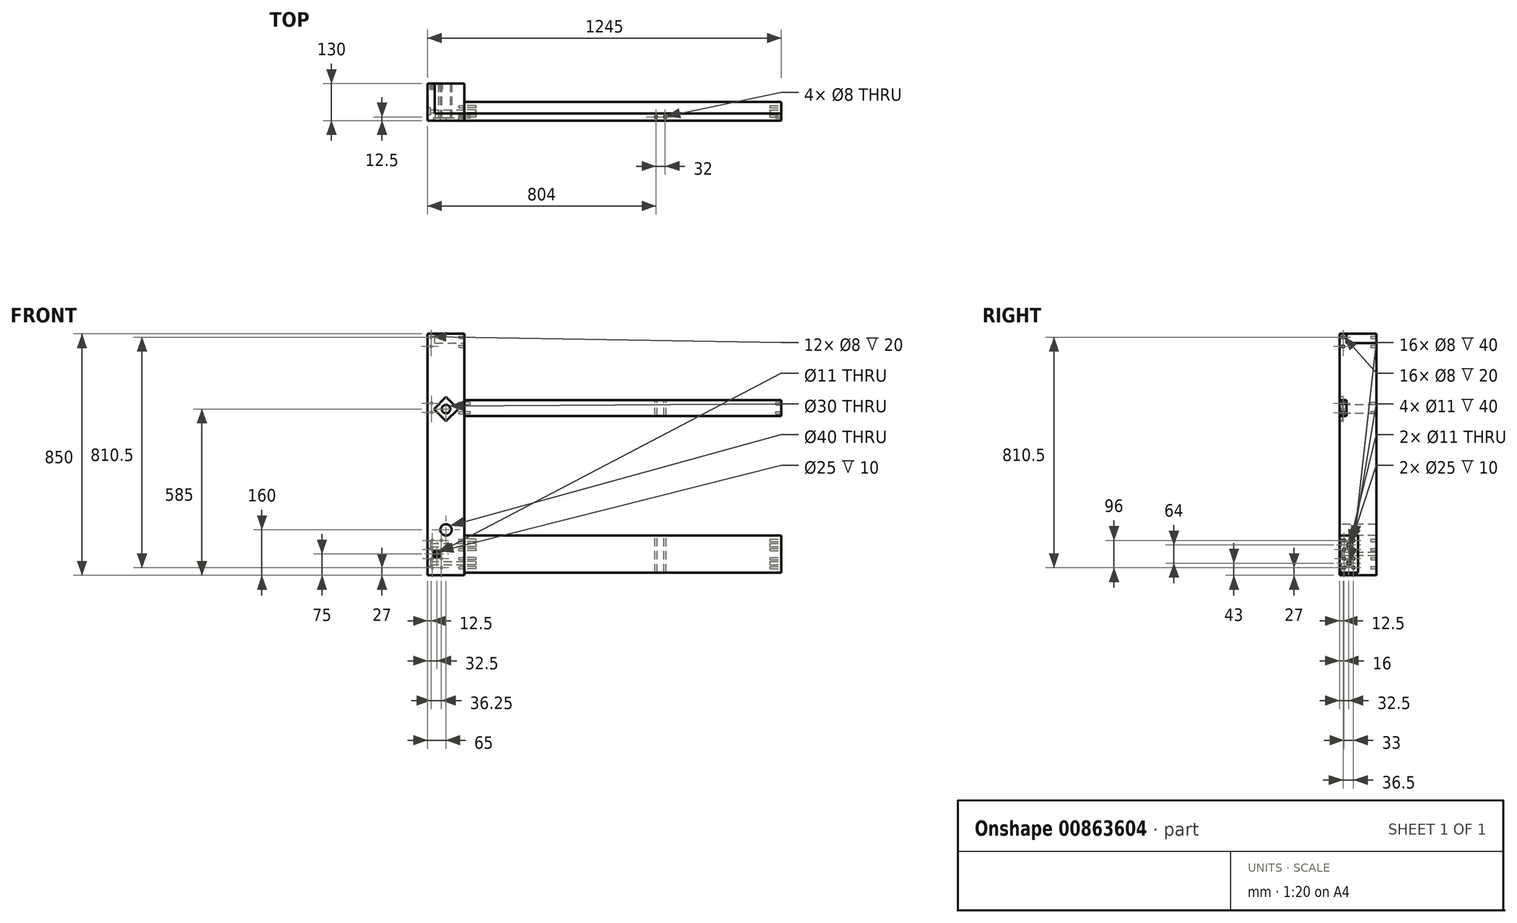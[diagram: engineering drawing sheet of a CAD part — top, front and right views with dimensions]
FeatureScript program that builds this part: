
annotation { "Feature Type Name" : "Feature", "Feature Type Description" : "" }
export const myFeature = defineFeature(function(context is Context, id is Id, definition is map)
    precondition{}
    {
        {
            var Q0;
            Q0=qCreatedBy(makeId("Top.planeOp"),FACE);
            var sketch = newSketch(context, id + "F0", { "sketchPlane" : qUnion([Q0])});
            skLineSegment(sketch, "E0.bottom", {"start": v(0, 0) * mm, "end": v(130, 0) * mm});
            skLineSegment(sketch, "E0.top", {"start": v(0, -130) * mm, "end": v(130, -130) * mm});
            skLineSegment(sketch, "E0.left", {"start": v(0, 0) * mm, "end": v(0, -130) * mm});
            skLineSegment(sketch, "E0.right", {"start": v(130, 0) * mm, "end": v(130, -130) * mm});
            skSolve(sketch);
        }
        {
            var Q0;
            Q0 = qSketchRegion(id + "F0", true);
            extrude(context, id + "F1", {"entities" : qUnion([Q0]), "depth" : 850 * mm, "offsetDistance" : 25 * mm});
        }
        {
            var Q0;
            Q0=makeQuery(id+"F1.opExtrude","SWEPT_FACE",FACE,{"disambiguationData":[OSD([sQuery(id+"F0.wireOp",EDGE,"E0.top")])]});
            var sketch = newSketch(context, id + "F2", { "sketchPlane" : qUnion([Q0])});
            skCircle(sketch, "E1", {"center": v(65, 585) * mm, "radius": 15 * mm});
            skPoint(sketch, "E1.centerSnap0", {"position": v(65, 850) * mm});
            skCircle(sketch, "E2", {"center": v(65, 160) * mm, "radius": 20 * mm});
            skCircle(sketch, "E3", {"center": v(32.5, 75) * mm, "radius": 5.5 * mm});
            skSolve(sketch);
        }
        {
            var Q0;
            Q0 = qSketchRegion(id + "F2", true);
            extrude(context, id + "F3", {"entities" : qUnion([Q0]), "operationType" : NewBodyOperationType.REMOVE, "endBound" : BoundingType.THROUGH_ALL, "oppositeDirection" : true, "depth" : 25 * mm, "offsetDistance" : 25 * mm});
        }
        {
            var Q0;
            Q0=makeQuery(id+"F1.opExtrude","SWEPT_FACE",FACE,{"disambiguationData":[OSD([sQuery(id+"F0.wireOp",EDGE,"E0.right")])]});
            var sketch = newSketch(context, id + "F4", { "sketchPlane" : qUnion([Q0])});
            skLineSegment(sketch, "E4.bottom", {"start": v(0, 850) * mm, "end": v(-105, 850) * mm, "construction": true});
            skLineSegment(sketch, "E4.top", {"start": v(0, 817) * mm, "end": v(-105, 817) * mm, "construction": true});
            skLineSegment(sketch, "E4.left", {"start": v(0, 850) * mm, "end": v(0, 817) * mm, "construction": true});
            skLineSegment(sketch, "E4.right", {"start": v(-105, 850) * mm, "end": v(-105, 817) * mm, "construction": true});
            skPoint(sketch, "E5", {"position": v(-97.5, 75) * mm});
            skLineSegment(sketch, "E6.bottom", {"start": v(-130, 14.05) * mm, "end": v(-65, 14.05) * mm, "construction": true});
            skLineSegment(sketch, "E6.top", {"start": v(-130, 144.05) * mm, "end": v(-65, 144.05) * mm, "construction": true});
            skLineSegment(sketch, "E6.left", {"start": v(-130, 14.05) * mm, "end": v(-130, 144.05) * mm, "construction": true});
            skLineSegment(sketch, "E6.right", {"start": v(-65, 14.05) * mm, "end": v(-65, 144.05) * mm, "construction": true});
            skCircle(sketch, "E7", {"center": v(-114, 123) * mm, "radius": 4 * mm, "construction": true});
            skCircle(sketch, "E8", {"center": v(-114, 91) * mm, "radius": 4 * mm, "construction": true});
            skLineSegment(sketch, "E9", {"start": v(-97.5, 14.05) * mm, "end": v(-97.5, 75) * mm, "construction": true});
            skLineSegment(sketch, "E10", {"start": v(-97.5, 75) * mm, "end": v(-65, 75) * mm, "construction": true});
            skPoint(sketch, "E10.endSnap0", {"position": v(-65, 79.05) * mm});
            skCircle(sketch, "E11.MirrorC", {"center": v(-114, 27) * mm, "radius": 4 * mm, "construction": true});
            skCircle(sketch, "E12.MirrorC", {"center": v(-114, 59) * mm, "radius": 4 * mm, "construction": true});
            skCircle(sketch, "E13.MirrorC", {"center": v(-81, 123) * mm, "radius": 4 * mm, "construction": true});
            skCircle(sketch, "E14.MirrorC", {"center": v(-81, 91) * mm, "radius": 4 * mm, "construction": true});
            skCircle(sketch, "E15.MirrorC", {"center": v(-81, 27) * mm, "radius": 4 * mm, "construction": true});
            skCircle(sketch, "E16.MirrorC", {"center": v(-81, 59) * mm, "radius": 4 * mm, "construction": true});
            skLineSegment(sketch, "E17", {"start": v(-114, 123) * mm, "end": v(-81, 91) * mm, "construction": true});
            skCircle(sketch, "E18", {"center": v(-97.5, 107) * mm, "radius": 5.5 * mm});
            skCircle(sketch, "E19.MirrorC", {"center": v(-97.5, 43) * mm, "radius": 5.5 * mm});
            skSolve(sketch);
        }
        {
            var Q0;
            Q0 = qSketchRegion(id + "F4", true);
            extrude(context, id + "F5", {"entities" : qUnion([Q0]), "operationType" : NewBodyOperationType.REMOVE, "oppositeDirection" : true, "depth" : 140 * mm, "offsetDistance" : 25 * mm});
        }
        {
            var Q0;
            Q0=makeQuery(id+"F1.opExtrude","CAP_FACE",FACE,{"disambiguationData":[OSD([sQuery(id+"F0.wireOp",EDGE,"E0.bottom"),sQuery(id+"F0.wireOp",EDGE,"E0.top"),sQuery(id+"F0.wireOp",EDGE,"E0.left"),sQuery(id+"F0.wireOp",EDGE,"E0.right")])],"isStart":false});
            var sketch = newSketch(context, id + "F6", { "sketchPlane" : qUnion([Q0])});
            skLineSegment(sketch, "E20.bottom", {"start": v(130, 0) * mm, "end": v(25, 0) * mm});
            skLineSegment(sketch, "E20.top", {"start": v(130, -105) * mm, "end": v(25, -105) * mm});
            skLineSegment(sketch, "E20.left", {"start": v(130, 0) * mm, "end": v(130, -105) * mm});
            skLineSegment(sketch, "E20.right", {"start": v(25, 0) * mm, "end": v(25, -105) * mm});
            skSolve(sketch);
        }
        {
            var Q0;
            Q0 = qSketchRegion(id + "F6", true);
            extrude(context, id + "F7", {"entities" : qUnion([Q0]), "operationType" : NewBodyOperationType.REMOVE, "oppositeDirection" : true, "depth" : 33 * mm, "offsetDistance" : 25 * mm});
        }
        {
            var Q0;
            Q0=makeQuery(id+"F4.imprint","IMPRINT",FACE,{"disambiguationData":[TD([[makeQuery(id+"F4.imprint","IMPRINT",EDGE,{"derivedFrom":sQuery(id+"F4.wireOp",EDGE,"E18")}),-1.0]])]});
            var sketch = newSketch(context, id + "F8", { "sketchPlane" : qUnion([Q0])});
            skCircle(sketch, "E21.0", {"center": v(-114, 123) * mm, "radius": 4 * mm});
            skCircle(sketch, "E22.0", {"center": v(-81, 123) * mm, "radius": 4 * mm});
            skCircle(sketch, "E23.0", {"center": v(-114, 91) * mm, "radius": 4 * mm});
            skCircle(sketch, "E24.0", {"center": v(-81, 91) * mm, "radius": 4 * mm});
            skCircle(sketch, "E25.0", {"center": v(-114, 59) * mm, "radius": 4 * mm});
            skCircle(sketch, "E26.0", {"center": v(-81, 59) * mm, "radius": 4 * mm});
            skCircle(sketch, "E27.0", {"center": v(-114, 27) * mm, "radius": 4 * mm});
            skCircle(sketch, "E28.0", {"center": v(-81, 27) * mm, "radius": 4 * mm});
            skLineSegment(sketch, "E29.bottom", {"start": v(0, 598) * mm, "end": v(-105, 598) * mm, "construction": true});
            skLineSegment(sketch, "E29.top", {"start": v(0, 617) * mm, "end": v(-105, 617) * mm, "construction": true});
            skLineSegment(sketch, "E29.left", {"start": v(0, 598) * mm, "end": v(0, 617) * mm, "construction": true});
            skLineSegment(sketch, "E29.right", {"start": v(-105, 598) * mm, "end": v(-105, 617) * mm, "construction": true});
            skCircle(sketch, "E30", {"center": v(-117.5, 837.5) * mm, "radius": 4 * mm});
            skCircle(sketch, "E31", {"center": v(-117.5, 805.5) * mm, "radius": 4 * mm});
            skCircle(sketch, "E32", {"center": v(-117.5, 604.5) * mm, "radius": 4 * mm});
            skCircle(sketch, "E33", {"center": v(-117.5, 572.5) * mm, "radius": 4 * mm});
            skLineSegment(sketch, "E34", {"start": v(-130, 793) * mm, "end": v(-105, 793) * mm, "construction": true});
            skSolve(sketch);
        }
        {
            var Q0;
            Q0 = qSketchRegion(id + "F8", true);
            extrude(context, id + "F9", {"entities" : qUnion([Q0]), "operationType" : NewBodyOperationType.REMOVE, "oppositeDirection" : true, "depth" : 20 * mm, "offsetDistance" : 25 * mm});
        }
        {
            var Q0;
            Q0=makeQuery(id+"F1.opExtrude","SWEPT_FACE",FACE,{"disambiguationData":[OSD([sQuery(id+"F0.wireOp",EDGE,"E0.bottom")])]});
            var sketch = newSketch(context, id + "F10", { "sketchPlane" : qUnion([Q0])});
            skLineSegment(sketch, "E35", {"start": v(-32.5, 75) * mm, "end": v(0, 75) * mm, "construction": true});
            skLineSegment(sketch, "E36", {"start": v(-32.5, 75) * mm, "end": v(-32.5, 0) * mm, "construction": true});
            skCircle(sketch, "E37", {"center": v(-16.25, 123) * mm, "radius": 4 * mm});
            skCircle(sketch, "E38", {"center": v(-16.25, 91) * mm, "radius": 4 * mm});
            skLineSegment(sketch, "E39", {"start": v(-16.25, 123) * mm, "end": v(-110, 123) * mm, "construction": true});
            skLineSegment(sketch, "E40", {"start": v(-16.25, 91) * mm, "end": v(-16.25, 75) * mm, "construction": true});
            skCircle(sketch, "E41.MirrorC", {"center": v(-48.75, 123) * mm, "radius": 4 * mm});
            skCircle(sketch, "E42.MirrorC", {"center": v(-48.75, 91) * mm, "radius": 4 * mm});
            skCircle(sketch, "E43.MirrorC", {"center": v(-48.75, 27) * mm, "radius": 4 * mm});
            skCircle(sketch, "E44.MirrorC", {"center": v(-16.25, 27) * mm, "radius": 4 * mm});
            skCircle(sketch, "E45.MirrorC", {"center": v(-16.25, 59) * mm, "radius": 4 * mm});
            skCircle(sketch, "E46.MirrorC", {"center": v(-48.75, 59) * mm, "radius": 4 * mm});
            skLineSegment(sketch, "E47", {"start": v(0, 837.5) * mm, "end": v(-110, 837.5) * mm, "construction": true});
            skLineSegment(sketch, "E48", {"start": v(-12.5, 850) * mm, "end": v(-12.5, 837.5) * mm, "construction": true});
            skCircle(sketch, "E49", {"center": v(-12.5, 837.5) * mm, "radius": 4 * mm});
            skCircle(sketch, "E50", {"center": v(-12.5, 805.5) * mm, "radius": 4 * mm});
            skCircle(sketch, "E51.0.1.0", {"center": v(-14.23, 605.5) * mm, "radius": 4 * mm});
            skCircle(sketch, "E51.0.1.1", {"center": v(-14.23, 573.5) * mm, "radius": 4 * mm});
            skLineSegment(sketch, "E51.direction1", {"start": v(-12.5, 805.5) * mm, "end": v(12.5, 805.5) * mm, "construction": true});
            skLineSegment(sketch, "E51.direction2", {"start": v(-12.5, 805.5) * mm, "end": v(-14.23, 573.5) * mm, "construction": true});
            skSolve(sketch);
        }
        {
            var Q0;
            Q0 = qSketchRegion(id + "F10", true);
            extrude(context, id + "F11", {"entities" : qUnion([Q0]), "operationType" : NewBodyOperationType.REMOVE, "oppositeDirection" : true, "depth" : 20 * mm, "offsetDistance" : 25 * mm});
        }
        {
            var Q0;
            Q0=makeQuery(id+"F1.opExtrude","SWEPT_FACE",FACE,{"disambiguationData":[OSD([sQuery(id+"F0.wireOp",EDGE,"E0.top")])]});
            var sketch = newSketch(context, id + "F12", { "sketchPlane" : qUnion([Q0])});
            skLineSegment(sketch, "E52.bottom", {"start": v(65, 542.57) * mm, "end": v(22.57, 585) * mm});
            skLineSegment(sketch, "E52.top", {"start": v(107.43, 585) * mm, "end": v(65, 627.43) * mm});
            skLineSegment(sketch, "E52.left", {"start": v(65, 542.57) * mm, "end": v(107.43, 585) * mm});
            skLineSegment(sketch, "E52.right", {"start": v(22.57, 585) * mm, "end": v(65, 627.43) * mm});
            skPoint(sketch, "E52.middle", {"position": v(65, 585) * mm});
            skCircle(sketch, "E53", {"center": v(32.5, 75) * mm, "radius": 12.5 * mm});
            skSolve(sketch);
        }
        {
            var Q0;
            Q0 = qSketchRegion(id + "F12", true);
            extrude(context, id + "F13", {"entities" : qUnion([Q0]), "operationType" : NewBodyOperationType.REMOVE, "oppositeDirection" : true, "depth" : 10 * mm, "offsetDistance" : 25 * mm});
        }
        {
            var Q0;
            Q0=makeQuery(id+"F1.opExtrude","SWEPT_FACE",FACE,{"disambiguationData":[OSD([sQuery(id+"F0.wireOp",EDGE,"E0.left")])]});
            var sketch = newSketch(context, id + "F14", { "sketchPlane" : qUnion([Q0])});
            skCircle(sketch, "E54", {"center": v(97.5, 107) * mm, "radius": 12.5 * mm});
            skCircle(sketch, "E55", {"center": v(97.5, 43) * mm, "radius": 12.5 * mm});
            skSolve(sketch);
        }
        {
            var Q0;
            Q0 = qSketchRegion(id + "F14", true);
            extrude(context, id + "F15", {"entities" : qUnion([Q0]), "operationType" : NewBodyOperationType.REMOVE, "oppositeDirection" : true, "depth" : 10 * mm, "offsetDistance" : 25 * mm});
        }
        {
            var Q0;
            Q0=makeQuery(id+"F1.opExtrude","SWEPT_FACE",FACE,{"disambiguationData":[OSD([sQuery(id+"F0.wireOp",EDGE,"E0.right")])]});
            var sketch = newSketch(context, id + "F16", { "sketchPlane" : qUnion([Q0])});
            skLineSegment(sketch, "E56.bottom", {"start": v(-130, 10) * mm, "end": v(-65, 10) * mm});
            skLineSegment(sketch, "E56.top", {"start": v(-130, 140) * mm, "end": v(-65, 140) * mm});
            skLineSegment(sketch, "E56.left", {"start": v(-130, 10) * mm, "end": v(-130, 140) * mm});
            skLineSegment(sketch, "E56.right", {"start": v(-65, 10) * mm, "end": v(-65, 140) * mm});
            skSolve(sketch);
        }
        {
            var Q0;
            Q0 = qSketchRegion(id + "F16", true);
            extrude(context, id + "F17", {"entities" : qUnion([Q0]), "depth" : 1115 * mm, "offsetDistance" : 25 * mm});
        }
        {
            var Q0;
            Q0=makeQuery(id+"F17.opExtrude","CAP_FACE",FACE,{"disambiguationData":[OSD([sQuery(id+"F16.wireOp",EDGE,"E56.bottom"),sQuery(id+"F16.wireOp",EDGE,"E56.top"),sQuery(id+"F16.wireOp",EDGE,"E56.left"),sQuery(id+"F16.wireOp",EDGE,"E56.right")])],"isStart":false});
            var sketch = newSketch(context, id + "F18", { "sketchPlane" : qUnion([Q0])});
            skCircle(sketch, "E57.0", {"center": v(-114, 123) * mm, "radius": 4 * mm});
            skCircle(sketch, "E58.0", {"center": v(-81, 123) * mm, "radius": 4 * mm});
            skCircle(sketch, "E59.0", {"center": v(-81, 91) * mm, "radius": 4 * mm});
            skCircle(sketch, "E60.0", {"center": v(-114, 91) * mm, "radius": 4 * mm});
            skCircle(sketch, "E61.0", {"center": v(-114, 59) * mm, "radius": 4 * mm});
            skCircle(sketch, "E62.0", {"center": v(-81, 59) * mm, "radius": 4 * mm});
            skCircle(sketch, "E63.0", {"center": v(-81, 27) * mm, "radius": 4 * mm});
            skCircle(sketch, "E64.0", {"center": v(-114, 27) * mm, "radius": 4 * mm});
            skCircle(sketch, "E65.0", {"center": v(-97.5, 43) * mm, "radius": 5.5 * mm});
            skCircle(sketch, "E66.0", {"center": v(-97.5, 107) * mm, "radius": 5.5 * mm});
            skSolve(sketch);
        }
        {
            var Q0;
            Q0 = qSketchRegion(id + "F18", true);
            extrude(context, id + "F19", {"entities" : qUnion([Q0]), "operationType" : NewBodyOperationType.REMOVE, "oppositeDirection" : true, "depth" : 40 * mm, "offsetDistance" : 25 * mm});
        }
        {
            var Q0;
            Q0=makeQuery(id+"F17.opExtrude","CAP_FACE",FACE,{"disambiguationData":[OSD([sQuery(id+"F16.wireOp",EDGE,"E56.bottom"),sQuery(id+"F16.wireOp",EDGE,"E56.top"),sQuery(id+"F16.wireOp",EDGE,"E56.left"),sQuery(id+"F16.wireOp",EDGE,"E56.right")])],"isStart":true});
            var sketch = newSketch(context, id + "F20", { "sketchPlane" : qUnion([Q0])});
            skCircle(sketch, "E67.0", {"center": v(81, 123) * mm, "radius": 4 * mm});
            skCircle(sketch, "E68.0", {"center": v(97.5, 107) * mm, "radius": 5.5 * mm});
            skCircle(sketch, "E69.0", {"center": v(114, 123) * mm, "radius": 4 * mm});
            skCircle(sketch, "E70.0", {"center": v(114, 91) * mm, "radius": 4 * mm});
            skCircle(sketch, "E71.0", {"center": v(114, 59) * mm, "radius": 4 * mm});
            skCircle(sketch, "E72.0", {"center": v(114, 27) * mm, "radius": 4 * mm});
            skCircle(sketch, "E73.0", {"center": v(97.5, 43) * mm, "radius": 5.5 * mm});
            skCircle(sketch, "E74.0", {"center": v(81, 27) * mm, "radius": 4 * mm});
            skCircle(sketch, "E75.0", {"center": v(81, 59) * mm, "radius": 4 * mm});
            skCircle(sketch, "E76.0", {"center": v(81, 91) * mm, "radius": 4 * mm});
            skSolve(sketch);
        }
        {
            var Q0;
            Q0 = qSketchRegion(id + "F20", true);
            extrude(context, id + "F21", {"entities" : qUnion([Q0]), "operationType" : NewBodyOperationType.REMOVE, "oppositeDirection" : true, "depth" : 40 * mm, "offsetDistance" : 25 * mm});
        }
        {
            var Q0;
            Q0=makeQuery(id+"F17.opExtrude","SWEPT_FACE",FACE,{"disambiguationData":[OSD([sQuery(id+"F16.wireOp",EDGE,"E56.top")])]});
            var sketch = newSketch(context, id + "F22", { "sketchPlane" : qUnion([Q0])});
            skLineSegment(sketch, "E77", {"start": v(820, -65) * mm, "end": v(820, -130) * mm, "construction": true});
            skCircle(sketch, "E78", {"center": v(804, -117.5) * mm, "radius": 4 * mm});
            skCircle(sketch, "E79.MirrorC", {"center": v(836, -117.5) * mm, "radius": 4 * mm});
            skSolve(sketch);
        }
        {
            var Q0;
            Q0 = qSketchRegion(id + "F22", true);
            extrude(context, id + "F23", {"entities" : qUnion([Q0]), "operationType" : NewBodyOperationType.REMOVE, "oppositeDirection" : true, "depth" : 20 * mm, "offsetDistance" : 25 * mm});
        }
        {
            var Q0;
            Q0=makeQuery(id+"F1.opExtrude","SWEPT_FACE",FACE,{"disambiguationData":[OSD([sQuery(id+"F0.wireOp",EDGE,"E0.right")])]});
            var sketch = newSketch(context, id + "F24", { "sketchPlane" : qUnion([Q0])});
            skLineSegment(sketch, "E80.bottom", {"start": v(-130, 617) * mm, "end": v(-105, 617) * mm});
            skLineSegment(sketch, "E80.top", {"start": v(-130, 560) * mm, "end": v(-105, 560) * mm});
            skLineSegment(sketch, "E80.left", {"start": v(-130, 617) * mm, "end": v(-130, 560) * mm});
            skLineSegment(sketch, "E80.right", {"start": v(-105, 617) * mm, "end": v(-105, 560) * mm});
            skLineSegment(sketch, "E81", {"start": v(-117.5, 604.5) * mm, "end": v(-117.5, 617) * mm, "construction": true});
            skSolve(sketch);
        }
        {
            var Q0;
            Q0 = qSketchRegion(id + "F24", true);
            extrude(context, id + "F25", {"entities" : qUnion([Q0]), "depth" : 1115 * mm, "offsetDistance" : 25 * mm});
        }
        {
            var Q0;
            Q0=makeQuery(id+"F25.opExtrude","CAP_FACE",FACE,{"disambiguationData":[OSD([sQuery(id+"F24.wireOp",EDGE,"E80.bottom"),sQuery(id+"F24.wireOp",EDGE,"E80.top"),sQuery(id+"F24.wireOp",EDGE,"E80.left"),sQuery(id+"F24.wireOp",EDGE,"E80.right")])],"isStart":false});
            var sketch = newSketch(context, id + "F26", { "sketchPlane" : qUnion([Q0])});
            skCircle(sketch, "E82.0", {"center": v(-117.5, 604.5) * mm, "radius": 4 * mm});
            skCircle(sketch, "E83.0", {"center": v(-117.5, 572.5) * mm, "radius": 4 * mm});
            skSolve(sketch);
        }
        {
            var Q0;
            Q0 = qSketchRegion(id + "F26", true);
            extrude(context, id + "F27", {"entities" : qUnion([Q0]), "operationType" : NewBodyOperationType.REMOVE, "oppositeDirection" : true, "depth" : 20 * mm, "offsetDistance" : 25 * mm});
        }
        {
            var Q0;
            Q0=makeQuery(id+"F25.opExtrude","CAP_FACE",FACE,{"disambiguationData":[OSD([sQuery(id+"F24.wireOp",EDGE,"E80.bottom"),sQuery(id+"F24.wireOp",EDGE,"E80.top"),sQuery(id+"F24.wireOp",EDGE,"E80.left"),sQuery(id+"F24.wireOp",EDGE,"E80.right")])],"isStart":true});
            var sketch = newSketch(context, id + "F28", { "sketchPlane" : qUnion([Q0])});
            skCircle(sketch, "E84.0", {"center": v(117.5, 604.5) * mm, "radius": 4 * mm});
            skCircle(sketch, "E85.0", {"center": v(117.5, 572.5) * mm, "radius": 4 * mm});
            skSolve(sketch);
        }
        {
            var Q0;
            Q0 = qSketchRegion(id + "F28", true);
            extrude(context, id + "F29", {"entities" : qUnion([Q0]), "operationType" : NewBodyOperationType.REMOVE, "oppositeDirection" : true, "depth" : 20 * mm, "offsetDistance" : 25 * mm});
        }
        {
            var Q0;
            Q0=makeQuery(id+"F25.opExtrude","SWEPT_FACE",FACE,{"disambiguationData":[OSD([sQuery(id+"F24.wireOp",EDGE,"E80.bottom")])]});
            var sketch = newSketch(context, id + "F30", { "sketchPlane" : qUnion([Q0])});
            skCircle(sketch, "E86.0", {"center": v(804, -117.5) * mm, "radius": 4 * mm});
            skCircle(sketch, "E87.0", {"center": v(836, -117.5) * mm, "radius": 4 * mm});
            skSolve(sketch);
        }
        {
            var Q0;
            Q0 = qSketchRegion(id + "F30", true);
            extrude(context, id + "F31", {"entities" : qUnion([Q0]), "operationType" : NewBodyOperationType.REMOVE, "endBound" : BoundingType.THROUGH_ALL, "oppositeDirection" : true, "depth" : 25 * mm, "offsetDistance" : 25 * mm});
        }
    });
